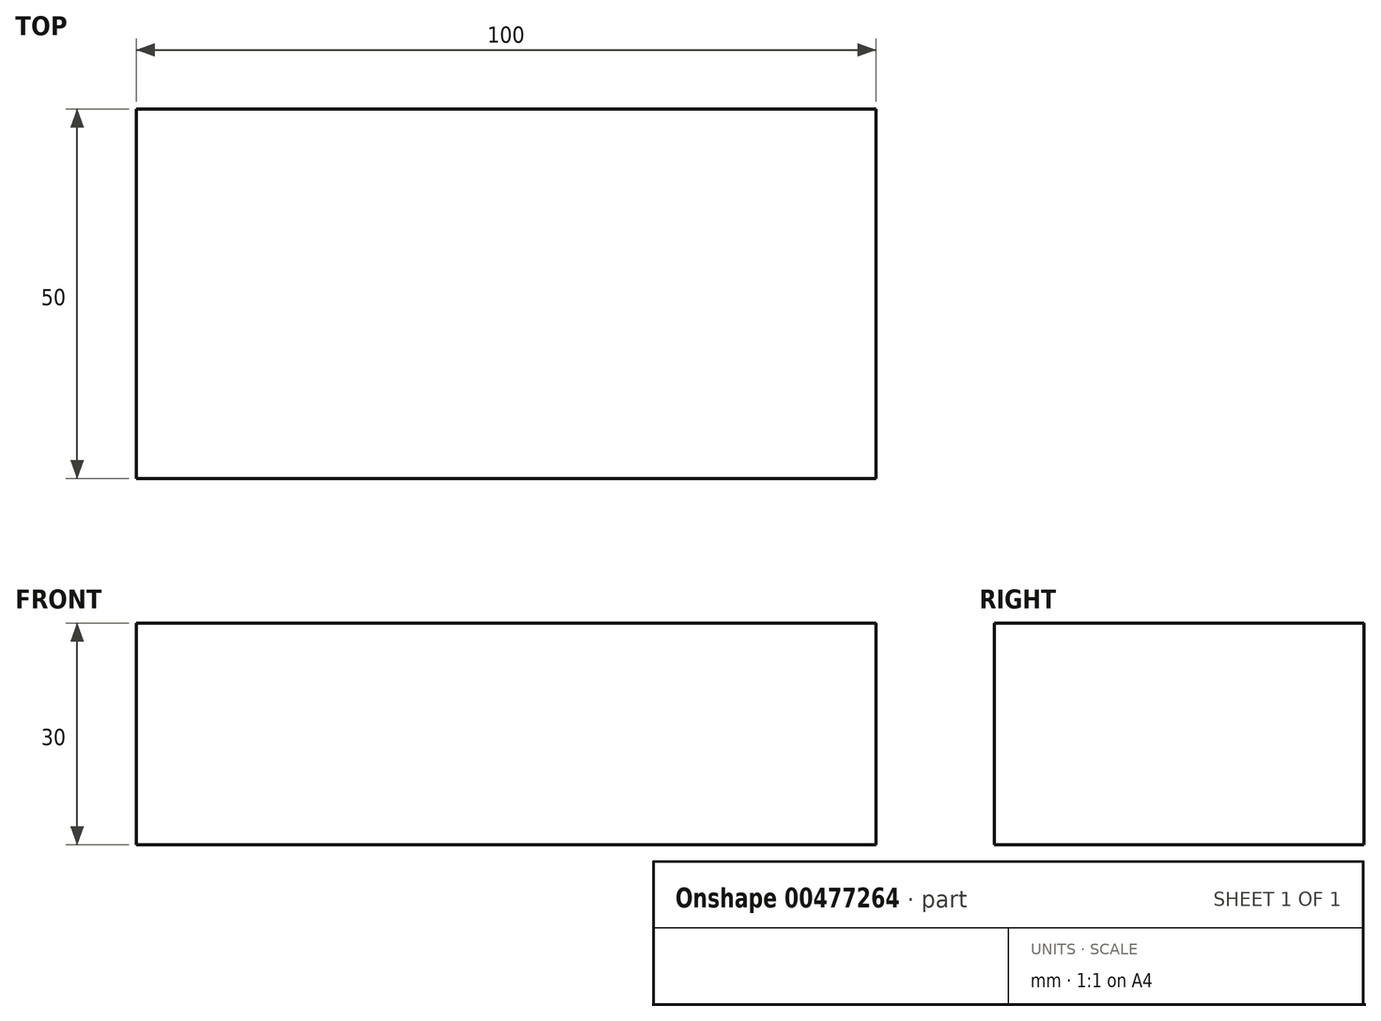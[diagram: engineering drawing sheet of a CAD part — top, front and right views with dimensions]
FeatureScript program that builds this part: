
annotation { "Feature Type Name" : "Feature", "Feature Type Description" : "" }
export const myFeature = defineFeature(function(context is Context, id is Id, definition is map)
    precondition{}
    {
        {
            var Q0;
            Q0=qCreatedBy(makeId("Top.planeOp"),FACE);
            var sketch = newSketch(context, id + "F0", { "sketchPlane" : qUnion([Q0])});
            skLineSegment(sketch, "E0.bottom", {"start": v(-70.1, -39.05) * mm, "end": v(29.9, -39.05) * mm});
            skLineSegment(sketch, "E0.top", {"start": v(-70.1, 10.95) * mm, "end": v(29.9, 10.95) * mm});
            skLineSegment(sketch, "E0.left", {"start": v(-70.1, -39.05) * mm, "end": v(-70.1, 10.95) * mm});
            skLineSegment(sketch, "E0.right", {"start": v(29.9, -39.05) * mm, "end": v(29.9, 10.95) * mm});
            skSolve(sketch);
        }
        {
            var Q0;
            Q0 = qSketchRegion(id + "F0", true);
            extrude(context, id + "F1", {"entities" : qUnion([Q0]), "depth" : 30 * mm});
        }
    });
